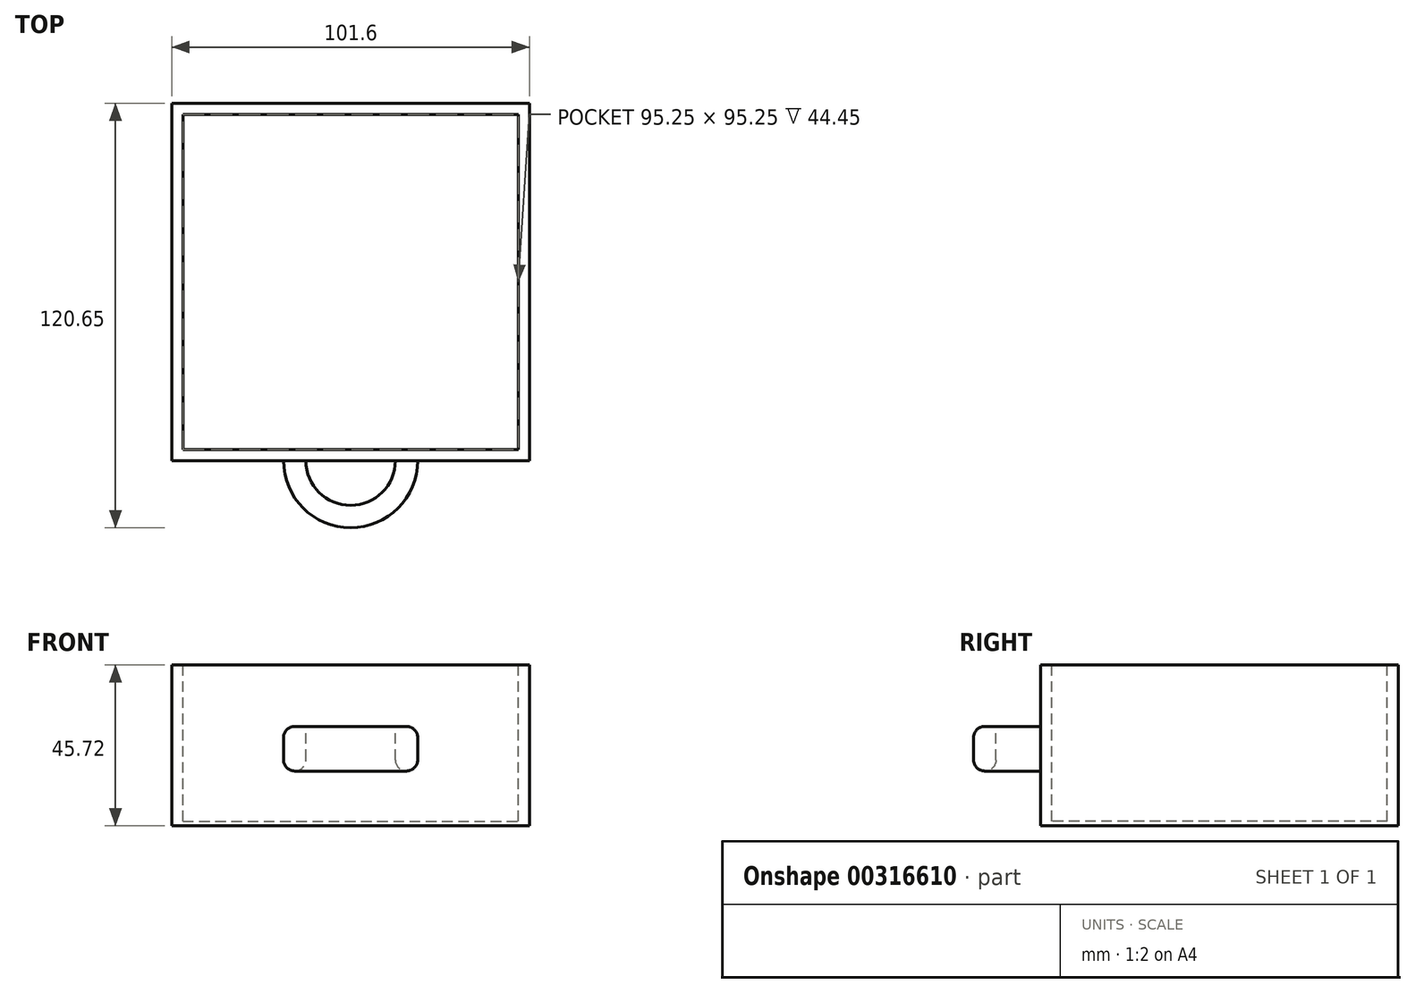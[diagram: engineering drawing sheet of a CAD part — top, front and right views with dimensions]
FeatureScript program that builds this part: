
annotation { "Feature Type Name" : "Feature", "Feature Type Description" : "" }
export const myFeature = defineFeature(function(context is Context, id is Id, definition is map)
    precondition{}
    {
        {
            var Q0;
            Q0=qCreatedBy(makeId("Front.planeOp"),FACE);
            var sketch = newSketch(context, id + "F0", { "sketchPlane" : qUnion([Q0])});
            skLineSegment(sketch, "E0.bottom", {"start": v(-33.41, 27.52) * mm, "end": v(68.19, 27.52) * mm});
            skLineSegment(sketch, "E0.top", {"start": v(-33.41, -18.2) * mm, "end": v(68.19, -18.2) * mm});
            skLineSegment(sketch, "E0.left", {"start": v(-33.41, 27.52) * mm, "end": v(-33.41, -18.2) * mm});
            skLineSegment(sketch, "E0.right", {"start": v(68.19, 27.52) * mm, "end": v(68.19, -18.2) * mm});
            skSolve(sketch);
        }
        {
            var Q0;
            Q0=qSketchRegion(id+"F0",true);
            extrude(context, id + "F1", {"entities" : qUnion([Q0]), "oppositeDirection" : true, "depth" : 101.6 * mm});
        }
        {
            var Q0;
            Q0=makeQuery(id+"F1.opExtrude","SWEPT_FACE",FACE,{"disambiguationData":[OSD([sQuery(id+"F0.wireOp",EDGE,"E0.bottom")])]});
            var sketch = newSketch(context, id + "F2", { "sketchPlane" : qUnion([Q0])});
            skLineSegment(sketch, "E1.bottom", {"start": v(-30.24, 98.43) * mm, "end": v(65.01, 98.43) * mm});
            skLineSegment(sketch, "E1.top", {"start": v(-30.24, 3.17) * mm, "end": v(65.01, 3.18) * mm});
            skLineSegment(sketch, "E1.left", {"start": v(-30.24, 98.43) * mm, "end": v(-30.24, 3.17) * mm});
            skLineSegment(sketch, "E1.right", {"start": v(65.01, 98.43) * mm, "end": v(65.01, 3.18) * mm});
            skSolve(sketch);
        }
        {
            var Q0;
            Q0=qSketchRegion(id+"F2",true);
            extrude(context, id + "F3", {"entities" : qUnion([Q0]), "operationType" : NewBodyOperationType.REMOVE, "oppositeDirection" : true, "depth" : 44.45 * mm});
        }
        {
            var Q0;
            Q0=makeQuery(id+"F1.opExtrude","CAP_FACE",FACE,{"disambiguationData":[OSD([sQuery(id+"F0.wireOp",EDGE,"E0.bottom"),sQuery(id+"F0.wireOp",EDGE,"E0.top"),sQuery(id+"F0.wireOp",EDGE,"E0.left"),sQuery(id+"F0.wireOp",EDGE,"E0.right")])],"isStart":true});
            var sketch = newSketch(context, id + "F4", { "sketchPlane" : qUnion([Q0])});
            skLineSegment(sketch, "E2.bottom", {"start": v(-1.66, 10.06) * mm, "end": v(36.44, 10.06) * mm});
            skLineSegment(sketch, "E2.top", {"start": v(-1.66, -2.64) * mm, "end": v(36.44, -2.64) * mm});
            skLineSegment(sketch, "E2.left", {"start": v(-1.66, 10.06) * mm, "end": v(-1.66, -2.64) * mm});
            skLineSegment(sketch, "E2.right", {"start": v(36.44, 10.06) * mm, "end": v(36.44, -2.64) * mm});
            skLineSegment(sketch, "E3", {"start": v(-1.66, 3.71) * mm, "end": v(36.44, 3.71) * mm});
            skLineSegment(sketch, "E4", {"start": v(17.39, 10.06) * mm, "end": v(17.39, -2.64) * mm});
            skSolve(sketch);
        }
        {
            var Q0;
            {var subQ3=sQuery(id+"F4.wireOp",EDGE,"E2.bottom");var subQ5=sQuery(id+"F4.wireOp",EDGE,"E2.left");var subQ7=makeQuery(id+"F4.imprint","INTERSECT",VERTEX,{"derivedFrom":[subQ3,subQ5]});Q0=makeQuery(id+"F4.imprint","IMPRINT",FACE,{"disambiguationData":[TD([[makeQuery(id+"F4.imprint","IMPRINT",EDGE,{"disambiguationData":[TD([[subQ7,-1.0]])],"derivedFrom":subQ3}),-1.0]])]});}
            var Q1;
            {var subQ3=sQuery(id+"F4.wireOp",EDGE,"E2.top");var subQ5=sQuery(id+"F4.wireOp",EDGE,"E2.left");var subQ7=makeQuery(id+"F4.imprint","INTERSECT",VERTEX,{"derivedFrom":[subQ3,subQ5]});Q1=makeQuery(id+"F4.imprint","IMPRINT",FACE,{"disambiguationData":[TD([[makeQuery(id+"F4.imprint","IMPRINT",EDGE,{"disambiguationData":[TD([[subQ7,-1.0]])],"derivedFrom":subQ3}),1.0]])]});}
            var Q2;
            Q2=sQuery(id+"F4.wireOp",EDGE,"E4");
            revolve(context, id + "F5", {"operationType" : NewBodyOperationType.ADD, "entities" : qUnion([Q0, Q1]), "axis" : qUnion([Q2]), "revolveType" : RevolveType.ONE_DIRECTION, "oppositeDirection" : true, "angle" : 180 * degree});
        }
        {
            var Q0;
            Q0=makeQuery(id+"F5.opRevolve","SWEPT_FACE",FACE,{"disambiguationData":[OSD([sQuery(id+"F4.wireOp",EDGE,"E2.bottom")])]});
            var sketch = newSketch(context, id + "F6", { "sketchPlane" : qUnion([Q0])});
            skLineSegment(sketch, "E5", {"start": v(4.69, 0) * mm, "end": v(30.09, 0) * mm});
            skArc(sketch, "E6", {"start": v(4.69, 0) * mm, "mid": v(17.39, -12.7) * mm, "end": v(30.09, 0) * mm});
            skSolve(sketch);
        }
        {
            var Q0;
            Q0=qSketchRegion(id+"F6",true);
            extrude(context, id + "F7", {"entities" : qUnion([Q0]), "operationType" : NewBodyOperationType.REMOVE, "oppositeDirection" : true, "depth" : 25.4 * mm});
        }
        {
            var Q0;
            Q0=makeQuery(id+"F5.opRevolve","SWEPT_EDGE",EDGE,{"disambiguationData":[OSD([sQuery(id+"F4.wireOp",EDGE,"E2.bottom"),sQuery(id+"F4.wireOp",EDGE,"E2.left")])]});
            var Q1;
            Q1=makeQuery(id+"F7.boolean.opBoolean","COPY",EDGE,{"derivedFrom":makeQuery(id+"F7.opExtrude","CAP_EDGE",EDGE,{"disambiguationData":[OSD([sQuery(id+"F6.wireOp",EDGE,"E6")])],"isStart":true})});
            var Q2;
            Q2=makeQuery(id+"F5.opRevolve","SWEPT_EDGE",EDGE,{"disambiguationData":[OSD([sQuery(id+"F4.wireOp",EDGE,"E2.top"),sQuery(id+"F4.wireOp",EDGE,"E2.left")])]});
            var Q3;
            Q3=makeQuery(id+"F7.boolean.opBoolean","INTERSECT",EDGE,{"derivedFrom":[makeQuery(id+"F5.opRevolve","SWEPT_FACE",FACE,{"disambiguationData":[OSD([sQuery(id+"F4.wireOp",EDGE,"E2.top")])]}),makeQuery(id+"F7.opExtrude","SWEPT_FACE",FACE,{"disambiguationData":[OSD([sQuery(id+"F6.wireOp",EDGE,"E6")])]})]});
            fillet(context, id + "F8", {"entities" : qUnion([Q0, Q1, Q2, Q3]), "radius" : 3.17 * mm, "tangentPropagation" : true, "allowEdgeOverflow" : false});
        }
    });
